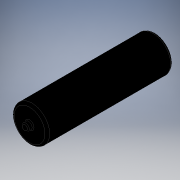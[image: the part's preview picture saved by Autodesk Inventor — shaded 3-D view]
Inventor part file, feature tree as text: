
AUTODESK INVENTOR PART (.ipt)
format: ipt  version: 2016 (Build 200138000, 138)  size: 122,368 bytes
history: native  units: mm
features: fillet x3, extrude x2, sketch x2
ambient origin geometry x8: Origin, YZ Plane, XZ Plane, XY Plane, X Axis, Y Axis, Z Axis, Center Point
bodies: Solid1 (feature_tree)
feature tree (7):
  extrude  "Extrusion1"  Depth=53.0mm
  extrude  "Extrusion2"  Depth=1.0mm
  fillet  "Fillet1"  Radius=0.4mm
  fillet  "Fillet2"  Radius=15.0mm
  fillet  "Fillet3"  Radius=1.0mm
  sketch  "Sketch1"  dims[d1=53.0mm d2=0.0mm d3=3.0mm]
  sketch  "Sketch2"  dims[d4=2.0mm d5=0.0mm d6=0.5mm d7=0.4mm d8=15.0mm d9=1.0mm]
